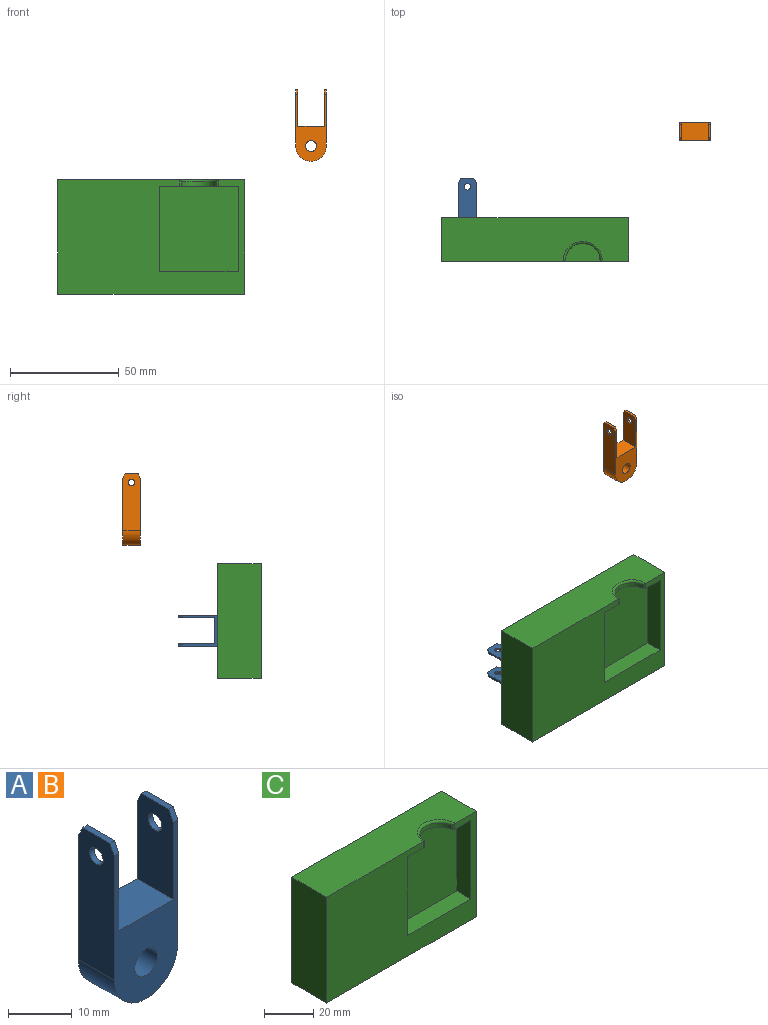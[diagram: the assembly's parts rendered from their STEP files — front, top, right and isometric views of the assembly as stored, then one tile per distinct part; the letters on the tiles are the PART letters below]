
ASSEMBLY  parts=3 mates=1
PART A: 17 faces, bbox 14x8x32.8 mm
  f0: plane 12x8mm, normal (0,0,1), area 96mm2, adj f1,f7,f9,f10
  f1: plane 16.79x8mm, normal (1,0,0), area 125.2mm2, adj f0,f2,f9,f10,f11,f12,f16
  f2: plane 6x1mm, normal (0,0,1), area 6mm2, adj f1,f3,f11,f12
  f3: plane 25.79x8mm, normal (-1,0,0), area 197.2mm2, adj f2,f4,f9,f10,f11,f12,f16
  f4: cylinder r=7mm len=14mm, axis (0,1,0), area 176mm2, adj f3,f5,f9,f10
  f5: plane 25.79x8mm, normal (1,0,0), area 197.2mm2, adj f4,f6,f9,f10,f13,f14,f15
  f6: plane 6x1mm, normal (0,0,1), area 6mm2, adj f5,f7,f13,f14
  f7: plane 16.79x8mm, normal (-1,0,0), area 125.2mm2, adj f0,f6,f9,f10,f13,f14,f15
  f8: cylinder r=2.5mm len=8mm, axis (0,1,0), area 125.7mm2, adj f9,f10
  f9: plane 30.79x14mm, normal (0,-1,0), area 213mm2, adj f0,f1,f3,f4,f5,f7,f8,f11
  f10: plane 30.79x14mm, normal (0,1,0), area 213mm2, adj f0,f1,f3,f4,f5,f7,f8,f12
  f11: plane 2x1mm, normal (0,-0.89,0.45), area 2.2mm2, adj f1,f2,f3,f9
  f12: plane 2x1mm, normal (0,0.89,0.45), area 2.2mm2, adj f1,f2,f3,f10
  f13: plane 2x1mm, normal (0,0.89,0.45), area 2.2mm2, adj f5,f6,f7,f10
  f14: plane 2x1mm, normal (0,-0.89,0.45), area 2.2mm2, adj f5,f6,f7,f9
  f15: cylinder r=1.5mm len=3mm, axis (1,0,0), area 9.4mm2, adj f5,f7
  f16: cylinder r=1.5mm len=3mm, axis (1,0,0), area 9.4mm2, adj f1,f3
PART B: same geometry as A
PART C: 27 faces, bbox 85.8x20x52.5 mm
  f0: plane 85.8x52.5mm, normal (0,1,0), area 4200.6mm2, adj f2,f5,f6,f7,f16,f17,f18,f19
  f1: plane 85.8x52.5mm, normal (0,-1,0), area 3028mm2, adj f2,f3,f4,f5,f6,f7,f8,f9
  f2: plane 85.8x20mm, normal (0,0,1), area 1588.8mm2, adj f0,f1,f5,f7,f14
  f3: plane 18.13x8mm, normal (0,0,-1), area 94.6mm2, adj f1,f10,f11,f12,f13
  f4: plane 18.13x8mm, normal (0,0,-1), area 94.6mm2, adj f1,f8,f11,f12,f15
  f5: plane 52.5x20mm, normal (-1,0,0), area 1050mm2, adj f0,f1,f2,f6
  f6: plane 85.8x20mm, normal (0,0,-1), area 1716mm2, adj f0,f1,f5,f7
  f7: plane 52.5x20mm, normal (1,0,0), area 1050mm2, adj f0,f1,f2,f6
  f8: plane 39.25x8mm, normal (1,0,0), area 314mm2, adj f1,f4,f9,f11
  f9: plane 36.25x8mm, normal (0,0,1), area 290mm2, adj f1,f8,f10,f11
  f10: plane 39.25x8mm, normal (-1,0,0), area 314mm2, adj f1,f3,f9,f11
  f11: plane 39.25x36.25mm, normal (0,-1,0), area 1422.8mm2, adj f3,f4,f8,f9,f10
  f12: cylinder r=8mm len=15.9mm, axis (0,0,1), area 46.7mm2, adj f3,f4,f13,f14,f15
  f13: cylinder r=1mm len=3mm, axis (0,0,1), area 3.8mm2, adj f1,f3,f12,f14
  f14: torus R=9mm, axis (0,0,-1), area 40.3mm2, adj f1,f2,f12,f13,f15
  f15: cylinder r=1mm len=3mm, axis (0,0,1), area 3.8mm2, adj f1,f4,f12,f14
  f16: plane 15.3x8.5mm, normal (0,0,-1), area 130mm2, adj f0,f17,f19,f20
  f17: plane 35.75x15.3mm, normal (-1,0,0), area 525.7mm2, adj f0,f16,f18,f20,f21
  f18: plane 15.3x8.5mm, normal (0,0,1), area 130mm2, adj f0,f17,f19,f20
  f19: plane 35.75x15.3mm, normal (1,0,0), area 525.7mm2, adj f0,f16,f18,f20,f24
  f20: plane 35.75x8.5mm, normal (0,1,0), area 303.9mm2, adj f16,f17,f18,f19
  f21: cylinder r=2.6mm len=5.2mm, axis (1,0,0), area 8.2mm2, adj f17,f23
  f22: plane 4.2x4.2mm, normal (-1,0,0), area 13.9mm2, adj f23
  f23: torus R=2.1mm, axis (-1,0,0), area 11.9mm2, adj f21,f22
  f24: cylinder r=2.6mm len=5.2mm, axis (-1,0,0), area 8.2mm2, adj f19,f26
  f25: plane 4.2x4.2mm, normal (1,0,0), area 13.9mm2, adj f26
  f26: torus R=2.1mm, axis (1,0,0), area 11.9mm2, adj f24,f25
PLACE A rot(axis=(-0.58,-0.58,-0.58),120deg) t=(15.8,5.35,-33.01)mm
PLACE B t=(116.39,63.43,6.05)mm
PLACE C t=(0,0,-2.41)mm
MATE revolute A.f4 <-> C.f21  axis (1,0,0) through (15.8,12.35,-33.16)mm
